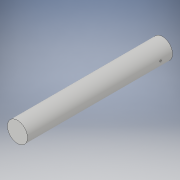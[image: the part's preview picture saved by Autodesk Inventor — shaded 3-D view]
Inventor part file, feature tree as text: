
AUTODESK INVENTOR PART (.ipt)
format: ipt  version: 2018 (Build 220112000, 112)  size: 111,616 bytes
history: native  units: in
note: dims shown in document units (in); Inventor stores cm internally (conversion verified against a paired STEP export)
features: sketch x3, extrude x2, plane x1, hole x1
ambient origin geometry x8: Origin, YZ Plane, XZ Plane, XY Plane, X Axis, Y Axis, Z Axis, Center Point
bodies: Solid1 (feature_tree)
feature tree (7):
  extrude  "Extrusion1"  Depth=72.0in TaperAngle=0.0deg
  plane  "Work Plane1"
  extrude  "Extrusion2"  Depth=12.0in TaperAngle=0.0deg
  hole  "Hole1"  [1 undecoded]
  sketch  "Sketch1"  dims[d0=10.0in d1=72.0in d2=0.0in]
  sketch  "Sketch2"  dims[d3=8.0in d4=12.0in d5=0.0in]
  sketch  "Sketch3"  dims[d6=1.0in d7=6.0in d8=0.865in d9=2.0in d10=0.375in d11=0.25in d12=0.5635in d13=2.625in d14=0.8108in]
note: 1 required parameter value undecoded (feature->parameter linkage not recoverable at this tier; creation-order binding heuristic only, values carry confidence <= 0.55)
